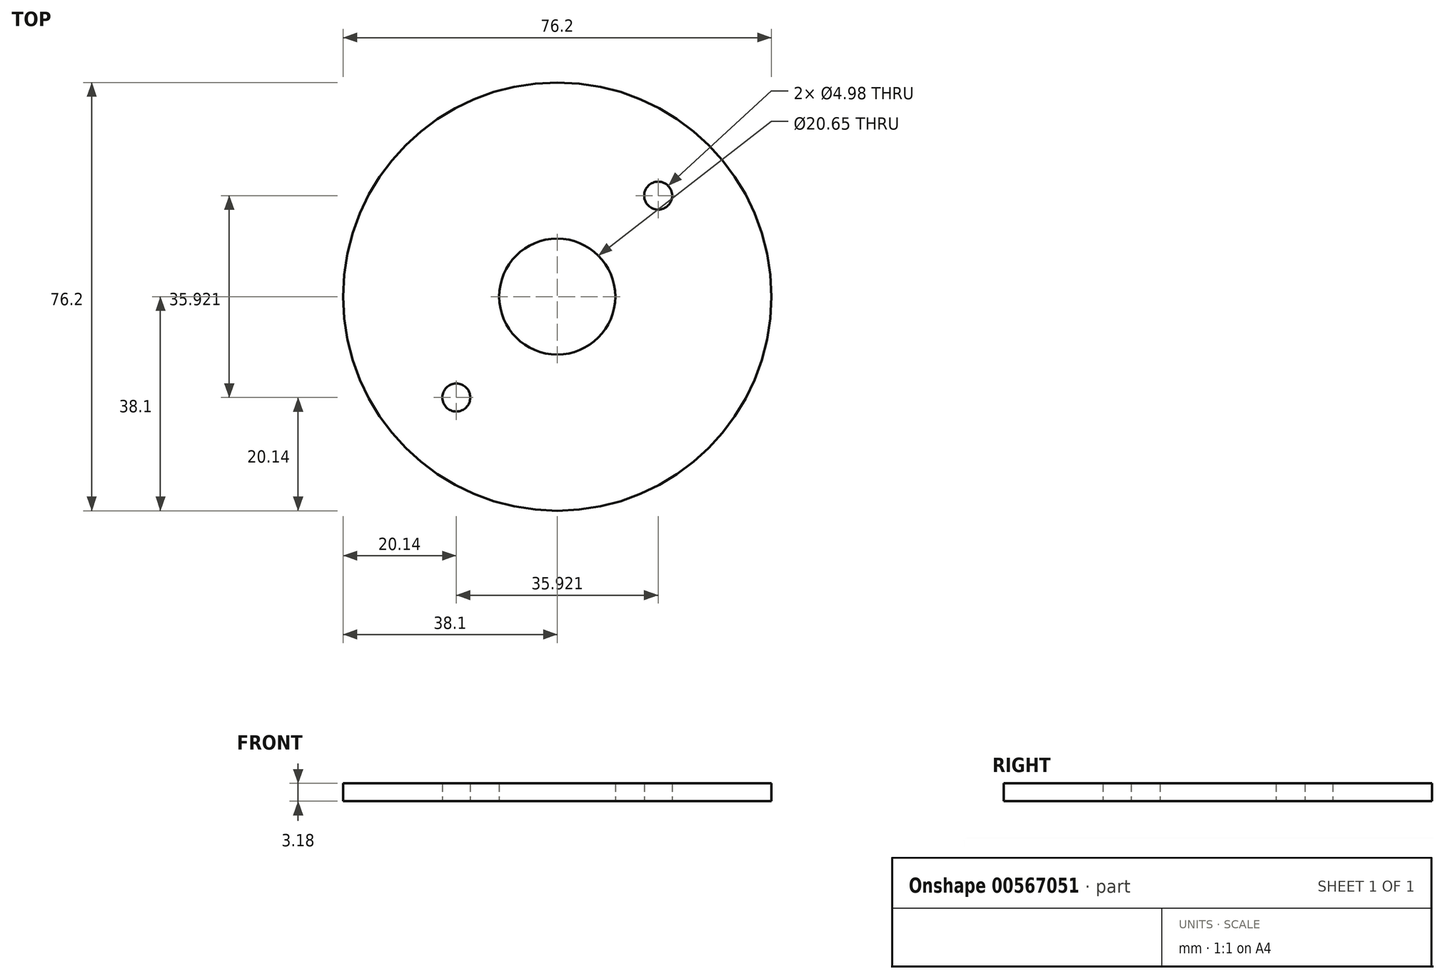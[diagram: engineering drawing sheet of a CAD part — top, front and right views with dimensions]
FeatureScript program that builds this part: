
annotation { "Feature Type Name" : "Feature", "Feature Type Description" : "" }
export const myFeature = defineFeature(function(context is Context, id is Id, definition is map)
    precondition{}
    {
        {
            var Q0;
            Q0=qCreatedBy(makeId("Top.planeOp"),FACE);
            var sketch = newSketch(context, id + "F0", { "sketchPlane" : qUnion([Q0])});
            skCircle(sketch, "E0", {"center": v(0, 0) * mm, "radius": 38.1 * mm});
            skCircle(sketch, "E1", {"center": v(0, 0) * mm, "radius": 25.4 * mm, "construction": true});
            skCircle(sketch, "E2", {"center": v(17.96, 17.96) * mm, "radius": 2.49 * mm});
            skLineSegment(sketch, "E3", {"start": v(17.96, 17.96) * mm, "end": v(-17.96, -17.96) * mm, "construction": true});
            skCircle(sketch, "E4", {"center": v(-17.96, -17.96) * mm, "radius": 2.49 * mm});
            skLineSegment(sketch, "E5", {"start": v(0, 0) * mm, "end": v(0, -25.4) * mm, "construction": true});
            skCircle(sketch, "E6", {"center": v(0, 0) * mm, "radius": 10.33 * mm});
            skSolve(sketch);
        }
        {
            var Q0;
            Q0=makeQuery(id+"F0.imprint","IMPRINT",FACE,{"disambiguationData":[TD([[makeQuery(id+"F0.imprint","IMPRINT",EDGE,{"derivedFrom":sQuery(id+"F0.wireOp",EDGE,"E0")}),1.0]])]});
            extrude(context, id + "F1", {"entities" : qUnion([Q0]), "depth" : 3.17 * mm, "offsetDistance" : 25.4 * mm});
        }
    });
